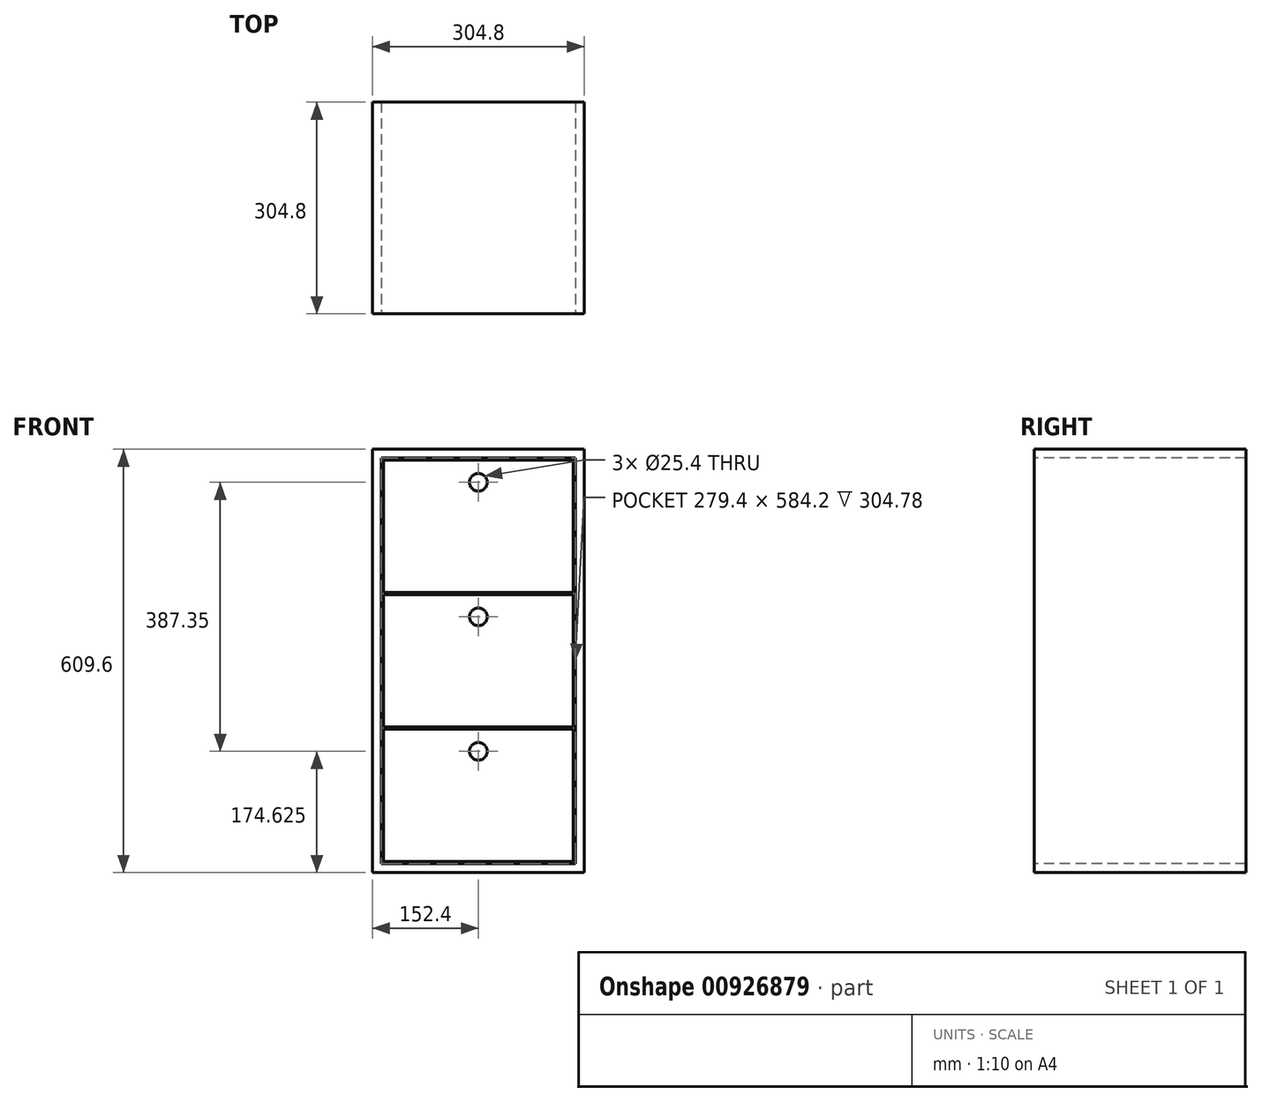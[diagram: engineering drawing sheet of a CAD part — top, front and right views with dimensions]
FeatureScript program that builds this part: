
annotation { "Feature Type Name" : "Feature", "Feature Type Description" : "" }
export const myFeature = defineFeature(function(context is Context, id is Id, definition is map)
    precondition{}
    {
        {
            assignVariable(context, id + "F0", {"name" : "depth", "anyValue" : 304.8 * mm});
        }
        {
            assignVariable(context, id + "F1", {"name" : "height", "anyValue" : 609.6 * mm});
        }
        {
            assignVariable(context, id + "F2", {"name" : "ply", "anyValue" : 1 / 50.8 * mm});
        }
        {
            var Q0;
            Q0=qCreatedBy(makeId("Top.planeOp"),FACE);
            var sketch = newSketch(context, id + "F3", { "sketchPlane" : qUnion([Q0])});
            skLineSegment(sketch, "E0.bottom", {"start": v(152.4, -152.4) * mm, "end": v(-152.4, -152.4) * mm});
            skLineSegment(sketch, "E0.top", {"start": v(152.4, 152.4) * mm, "end": v(-152.4, 152.4) * mm});
            skLineSegment(sketch, "E0.left", {"start": v(152.4, -152.4) * mm, "end": v(152.4, 152.4) * mm});
            skLineSegment(sketch, "E0.right", {"start": v(-152.4, -152.4) * mm, "end": v(-152.4, 152.4) * mm});
            skPoint(sketch, "E0.middle", {"position": v(0, 0) * mm});
            skSolve(sketch);
        }
        {
            var Q0;
            Q0=makeQuery(id+"F3.imprint","IMPRINT",FACE,{"disambiguationData":[TD([[makeQuery(id+"F3.imprint","IMPRINT",EDGE,{"derivedFrom":sQuery(id+"F3.wireOp",EDGE,"E0.bottom")}),-1.0]])]});
            extrude(context, id + "F4", {"entities" : qUnion([Q0]), "depth" : getVariable(context, 'height'), "offsetDistance" : 25.4 * mm});
        }
        {
            var Q0;
            Q0=makeQuery(id+"F4.opExtrude","SWEPT_FACE",FACE,{"disambiguationData":[OSD([sQuery(id+"F3.wireOp",EDGE,"E0.bottom")])]});
            var sketch = newSketch(context, id + "F5", { "sketchPlane" : qUnion([Q0])});
            skLineSegment(sketch, "E1.bottom", {"start": v(-139.7, 596.9) * mm, "end": v(139.7, 596.9) * mm});
            skLineSegment(sketch, "E1.top", {"start": v(-139.7, 12.7) * mm, "end": v(139.7, 12.7) * mm});
            skLineSegment(sketch, "E1.left", {"start": v(-139.7, 596.9) * mm, "end": v(-139.7, 12.7) * mm});
            skLineSegment(sketch, "E1.right", {"start": v(139.7, 596.9) * mm, "end": v(139.7, 12.7) * mm});
            skSolve(sketch);
        }
        {
            var Q0;
            Q0=makeQuery(id+"F5.imprint","IMPRINT",FACE,{"disambiguationData":[TD([[makeQuery(id+"F5.imprint","IMPRINT",EDGE,{"derivedFrom":sQuery(id+"F5.wireOp",EDGE,"E1.bottom")}),-1.0]])]});
            extrude(context, id + "F6", {"entities" : qUnion([Q0]), "operationType" : NewBodyOperationType.REMOVE, "oppositeDirection" : true, "depth" : getVariable(context, 'depth') - getVariable(context, 'ply'), "offsetDistance" : 25.4 * mm});
        }
        {
            var Q0;
            Q0=makeQuery(id+"F4.opExtrude","SWEPT_FACE",FACE,{"disambiguationData":[OSD([sQuery(id+"F3.wireOp",EDGE,"E0.bottom")])]});
            cPlane(context, id + "F7", {"entities" : qUnion([Q0]), "cplaneType" : CPlaneType.OFFSET, "offset" : 0 * mm, "width" : 152.4 * mm, "height" : 152.4 * mm});
        }
        {
            var Q0;
            Q0=qCreatedBy(id+"F7.planeOp",FACE);
            var sketch = newSketch(context, id + "F8", { "sketchPlane" : qUnion([Q0])});
            skLineSegment(sketch, "E2.bottom", {"start": v(-136.53, 15.87) * mm, "end": v(136.53, 15.87) * mm});
            skLineSegment(sketch, "E2.top", {"start": v(-136.53, 206.38) * mm, "end": v(136.52, 206.38) * mm});
            skLineSegment(sketch, "E2.left", {"start": v(-136.53, 15.88) * mm, "end": v(-136.53, 206.38) * mm});
            skLineSegment(sketch, "E2.right", {"start": v(136.53, 15.88) * mm, "end": v(136.53, 206.38) * mm});
            skLineSegment(sketch, "E3.0.1.0", {"start": v(-136.53, 400.05) * mm, "end": v(136.52, 400.05) * mm});
            skLineSegment(sketch, "E3.0.1.1", {"start": v(-136.53, 209.55) * mm, "end": v(-136.53, 400.05) * mm});
            skLineSegment(sketch, "E3.0.1.2", {"start": v(-136.52, 209.55) * mm, "end": v(136.52, 209.55) * mm});
            skLineSegment(sketch, "E3.0.1.3", {"start": v(136.53, 209.55) * mm, "end": v(136.53, 400.05) * mm});
            skLineSegment(sketch, "E3.0.2.0", {"start": v(-136.53, 593.72) * mm, "end": v(136.52, 593.72) * mm});
            skLineSegment(sketch, "E3.0.2.1", {"start": v(-136.53, 403.22) * mm, "end": v(-136.53, 593.72) * mm});
            skLineSegment(sketch, "E3.0.2.2", {"start": v(-136.53, 403.22) * mm, "end": v(136.52, 403.22) * mm});
            skLineSegment(sketch, "E3.0.2.3", {"start": v(136.53, 403.22) * mm, "end": v(136.52, 593.72) * mm});
            skLineSegment(sketch, "E3.direction1", {"start": v(-136.53, 206.38) * mm, "end": v(-112.71, 206.38) * mm, "construction": true});
            skLineSegment(sketch, "E3.direction2", {"start": v(-136.53, 206.38) * mm, "end": v(-136.53, 400.05) * mm, "construction": true});
            skCircle(sketch, "E4", {"center": v(0, 174.62) * mm, "radius": 12.7 * mm});
            skCircle(sketch, "E5.0.1.0", {"center": v(0, 368.3) * mm, "radius": 12.7 * mm});
            skCircle(sketch, "E5.0.2.0", {"center": v(0, 561.98) * mm, "radius": 12.7 * mm});
            skLineSegment(sketch, "E5.direction1", {"start": v(0, 174.62) * mm, "end": v(25.4, 174.62) * mm, "construction": true});
            skLineSegment(sketch, "E5.direction2", {"start": v(0, 174.62) * mm, "end": v(0, 368.3) * mm, "construction": true});
            skSolve(sketch);
        }
        {
            var Q0;
            Q0=makeQuery(id+"F8.imprint","IMPRINT",FACE,{"disambiguationData":[TD([[makeQuery(id+"F8.imprint","IMPRINT",EDGE,{"derivedFrom":sQuery(id+"F8.wireOp",EDGE,"E3.0.3.0")}),-1.0]])]});
            var Q1;
            Q1=makeQuery(id+"F8.imprint","IMPRINT",FACE,{"disambiguationData":[TD([[makeQuery(id+"F8.imprint","IMPRINT",EDGE,{"derivedFrom":sQuery(id+"F8.wireOp",EDGE,"E3.0.2.0")}),-1.0]])]});
            var Q2;
            Q2=makeQuery(id+"F8.imprint","IMPRINT",FACE,{"disambiguationData":[TD([[makeQuery(id+"F8.imprint","IMPRINT",EDGE,{"derivedFrom":sQuery(id+"F8.wireOp",EDGE,"E3.0.1.0")}),-1.0]])]});
            var Q3;
            Q3=makeQuery(id+"F8.imprint","IMPRINT",FACE,{"disambiguationData":[TD([[makeQuery(id+"F8.imprint","IMPRINT",EDGE,{"derivedFrom":sQuery(id+"F8.wireOp",EDGE,"E2.bottom")}),1.0]])]});
            var Q4;
            Q4=makeQuery(id+"F8.imprint","IMPRINT",FACE,{"disambiguationData":[TD([[makeQuery(id+"F8.imprint","IMPRINT",EDGE,{"derivedFrom":sQuery(id+"F8.wireOp",EDGE,"7e9bcb5c-a475-4690-9f18-2bcfa10e3da3.0.0.4")}),-1.0]])]});
            extrude(context, id + "F9", {"entities" : qUnion([Q0, Q1, Q2, Q3, Q4]), "oppositeDirection" : true, "depth" : getVariable(context, 'ply'), "offsetDistance" : 25.4 * mm});
        }
    });
